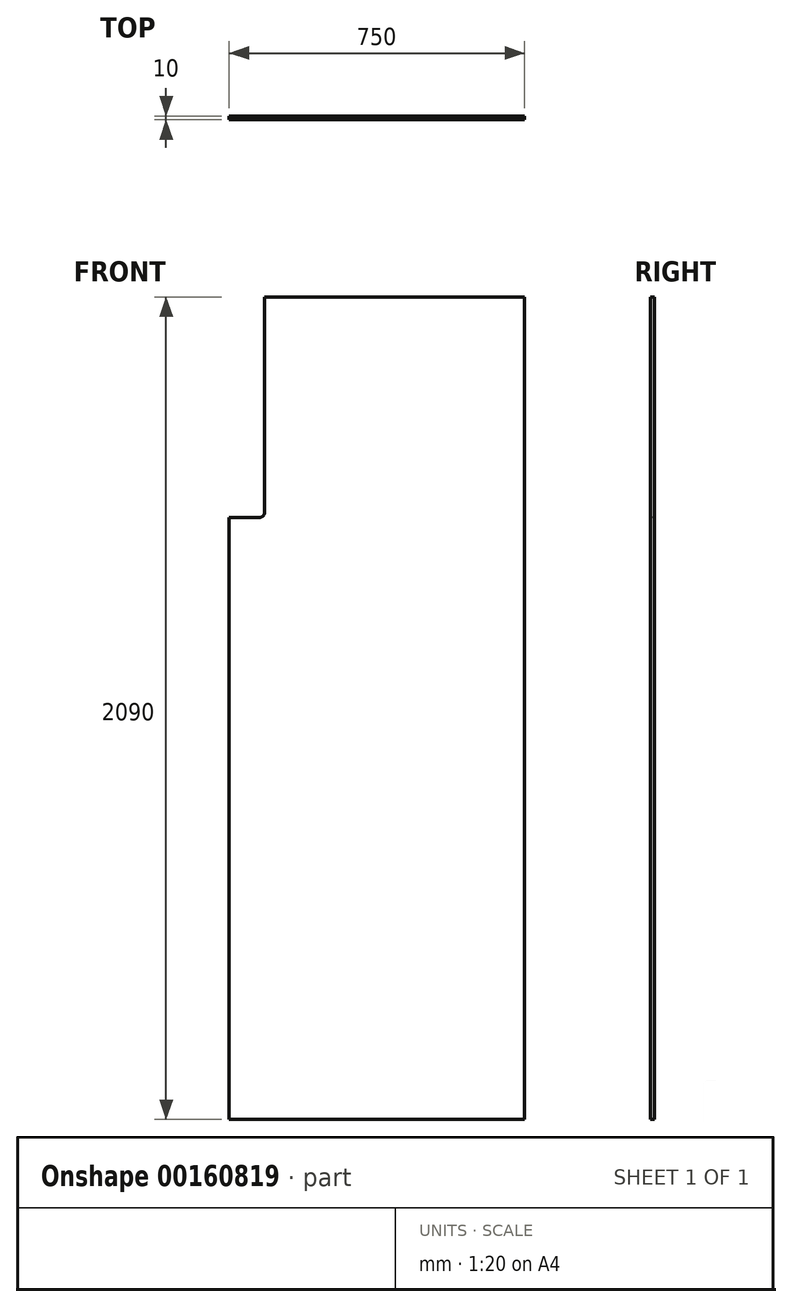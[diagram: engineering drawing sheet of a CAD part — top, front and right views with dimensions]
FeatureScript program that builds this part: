
annotation { "Feature Type Name" : "Feature", "Feature Type Description" : "" }
export const myFeature = defineFeature(function(context is Context, id is Id, definition is map)
    precondition{}
    {
        {
            var Q0;
            Q0=qCreatedBy(makeId("Front.planeOp"),FACE);
            var sketch = newSketch(context, id + "F0", { "sketchPlane" : qUnion([Q0])});
            skLineSegment(sketch, "E0.bottom", {"start": v(0, 0) * mm, "end": v(750, 0) * mm});
            skLineSegment(sketch, "E0.top", {"start": v(90, 2090) * mm, "end": v(750, 2090) * mm});
            skLineSegment(sketch, "E0.left", {"start": v(0, 0) * mm, "end": v(0, 1530) * mm});
            skLineSegment(sketch, "E0.right", {"start": v(750, 0) * mm, "end": v(750, 2090) * mm});
            skLineSegment(sketch, "E1.top", {"start": v(0, 1530) * mm, "end": v(77, 1530) * mm});
            skLineSegment(sketch, "E1.right", {"start": v(90, 2090) * mm, "end": v(90, 1543) * mm});
            skPoint(sketch, "E2.visualSharp", {"position": v(90, 1530) * mm});
            skArc(sketch, "E2.filletArc", {"start": v(77, 1530) * mm, "mid": v(86.2, 1533.8) * mm, "end": v(90, 1543) * mm});
            skSolve(sketch);
        }
        {
            var Q0;
            Q0=makeQuery(id+"F0.imprint","IMPRINT",FACE,{"disambiguationData":[TD([[makeQuery(id+"F0.imprint","IMPRINT",EDGE,{"derivedFrom":sQuery(id+"F0.wireOp",EDGE,"E0.bottom")}),1.0]])]});
            extrude(context, id + "F1", {"entities" : qUnion([Q0]), "oppositeDirection" : true, "depth" : 10 * mm});
        }
    });
